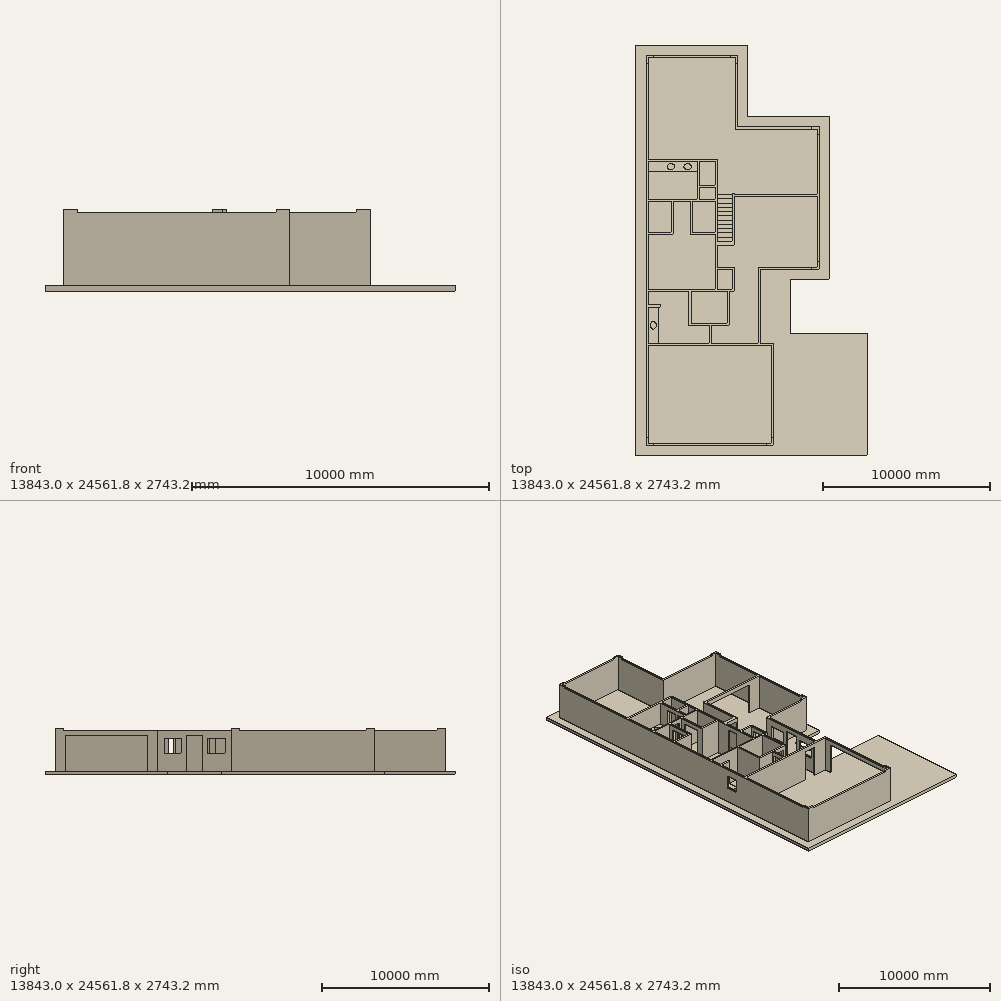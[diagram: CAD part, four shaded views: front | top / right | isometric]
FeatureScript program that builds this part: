
annotation { "Feature Type Name" : "Feature", "Feature Type Description" : "" }
export const myFeature = defineFeature(function(context is Context, id is Id, definition is map)
    precondition{}
    {
        {
            var Q0;
            Q0=qCreatedBy(makeId("Top.planeOp"),FACE);
            var sketch = newSketch(context, id + "F0", { "sketchPlane" : qUnion([Q0])});
            skLineSegment(sketch, "E0", {"start": v(0, 0) * mm, "end": v(7645.4, 0) * mm});
            skLineSegment(sketch, "E1", {"start": v(7645.4, 0) * mm, "end": v(7645.4, 6096) * mm});
            skLineSegment(sketch, "E2", {"start": v(7645.4, 6096) * mm, "end": v(6832.6, 6096) * mm});
            skLineSegment(sketch, "E3", {"start": v(6832.6, 6096) * mm, "end": v(6832.6, 10541) * mm});
            skLineSegment(sketch, "E4", {"start": v(6832.6, 10541) * mm, "end": v(10363.2, 10541) * mm});
            skLineSegment(sketch, "E5", {"start": v(10363.2, 10541) * mm, "end": v(10363.2, 19075.4) * mm});
            skLineSegment(sketch, "E6", {"start": v(10363.2, 19075.4) * mm, "end": v(5486.4, 19075.4) * mm});
            skLineSegment(sketch, "E7", {"start": v(5486.4, 19075.4) * mm, "end": v(5486.4, 23342.6) * mm});
            skLineSegment(sketch, "E8", {"start": v(5486.4, 23342.6) * mm, "end": v(0, 23342.6) * mm});
            skLineSegment(sketch, "E9", {"start": v(0, 23342.6) * mm, "end": v(0, 0) * mm});
            skSolve(sketch);
        }
        {
            var Q0;
            Q0 = qSketchRegion(id + "F0", true);
            extrude(context, id + "F1", {"entities" : qUnion([Q0]), "depth" : 2641.6 * mm});
        }
        {
            var Q0;
            Q0=qCreatedBy(makeId("Top.planeOp"),FACE);
            var sketch = newSketch(context, id + "F2", { "sketchPlane" : qUnion([Q0])});
            skLineSegment(sketch, "E10", {"start": v(-609.6, 23952.2) * mm, "end": v(-609.6, -609.6) * mm});
            skLineSegment(sketch, "E11", {"start": v(-609.6, -609.6) * mm, "end": v(13233.4, -609.6) * mm});
            skLineSegment(sketch, "E12", {"start": v(13233.4, -609.6) * mm, "end": v(13233.4, 6705.6) * mm});
            skLineSegment(sketch, "E13", {"start": v(13233.4, 6705.6) * mm, "end": v(8661.4, 6705.6) * mm});
            skLineSegment(sketch, "E14", {"start": v(8661.4, 6705.6) * mm, "end": v(8661.4, 9931.4) * mm});
            skLineSegment(sketch, "E15", {"start": v(8661.4, 9931.4) * mm, "end": v(10972.8, 9931.4) * mm});
            skLineSegment(sketch, "E16", {"start": v(10972.8, 9931.4) * mm, "end": v(10972.8, 19685) * mm});
            skLineSegment(sketch, "E17", {"start": v(10972.8, 19685) * mm, "end": v(6096, 19685) * mm});
            skLineSegment(sketch, "E18", {"start": v(6096, 19685) * mm, "end": v(6096, 23952.2) * mm});
            skLineSegment(sketch, "E19", {"start": v(6096, 23952.2) * mm, "end": v(-609.6, 23952.2) * mm});
            skSolve(sketch);
        }
        {
            var Q0;
            Q0 = qSketchRegion(id + "F2", true);
            extrude(context, id + "F3", {"entities" : qUnion([Q0]), "operationType" : NewBodyOperationType.ADD, "depth" : 203.2 * mm});
        }
        {
            var Q0;
            Q0=makeQuery(id+"F1.opExtrude","CAP_FACE",FACE,{"disambiguationData":[OSD([sQuery(id+"F0.wireOp",EDGE,"E0"),sQuery(id+"F0.wireOp",EDGE,"E1"),sQuery(id+"F0.wireOp",EDGE,"E2"),sQuery(id+"F0.wireOp",EDGE,"E3"),sQuery(id+"F0.wireOp",EDGE,"E4"),sQuery(id+"F0.wireOp",EDGE,"E5"),sQuery(id+"F0.wireOp",EDGE,"E6"),sQuery(id+"F0.wireOp",EDGE,"E7"),sQuery(id+"F0.wireOp",EDGE,"E8"),sQuery(id+"F0.wireOp",EDGE,"E9")])],"isStart":false});
            var sketch = newSketch(context, id + "F4", { "sketchPlane" : qUnion([Q0])});
            skLineSegment(sketch, "E20.bottom", {"start": v(127, 23215.6) * mm, "end": v(5359.4, 23215.6) * mm});
            skLineSegment(sketch, "E20.left", {"start": v(127, 23215.6) * mm, "end": v(127, 17119.6) * mm});
            skLineSegment(sketch, "E20.right", {"start": v(5359.4, 23215.6) * mm, "end": v(5359.4, 18948.4) * mm});
            skLineSegment(sketch, "E21.bottom", {"start": v(127, 5969) * mm, "end": v(7518.4, 5969) * mm});
            skLineSegment(sketch, "E21.top", {"start": v(127, 127) * mm, "end": v(7518.4, 127) * mm});
            skLineSegment(sketch, "E21.left", {"start": v(127, 5969) * mm, "end": v(127, 127) * mm});
            skLineSegment(sketch, "E21.right", {"start": v(7518.4, 5969) * mm, "end": v(7518.4, 127) * mm});
            skLineSegment(sketch, "E22", {"start": v(5359.4, 18948.4) * mm, "end": v(10236.2, 18948.4) * mm});
            skLineSegment(sketch, "E23", {"start": v(127, 17119.6) * mm, "end": v(4267.2, 17119.6) * mm});
            skLineSegment(sketch, "E24", {"start": v(4267.2, 17119.6) * mm, "end": v(4267.2, 10668) * mm});
            skLineSegment(sketch, "E25", {"start": v(4267.2, 10668) * mm, "end": v(5308.6, 10668) * mm});
            skLineSegment(sketch, "E26", {"start": v(10236.2, 10668) * mm, "end": v(10236.2, 14884.4) * mm});
            skLineSegment(sketch, "E27", {"start": v(5181.6, 15062.2) * mm, "end": v(5181.6, 11963.4) * mm});
            skLineSegment(sketch, "E28", {"start": v(5181.6, 11963.4) * mm, "end": v(5308.6, 11963.4) * mm});
            skLineSegment(sketch, "E29", {"start": v(5308.6, 11963.4) * mm, "end": v(5308.6, 14884.4) * mm});
            skLineSegment(sketch, "E30", {"start": v(5308.6, 14884.4) * mm, "end": v(10236.2, 14884.4) * mm});
            skLineSegment(sketch, "E31", {"start": v(5181.6, 15062.2) * mm, "end": v(5308.6, 15062.2) * mm});
            skLineSegment(sketch, "E32", {"start": v(5308.6, 15062.2) * mm, "end": v(5308.6, 15011.4) * mm});
            skLineSegment(sketch, "E33", {"start": v(5308.6, 15011.4) * mm, "end": v(10236.2, 15011.4) * mm});
            skLineSegment(sketch, "E34.trimOffspring", {"start": v(10236.2, 15011.4) * mm, "end": v(10236.2, 18948.4) * mm});
            skLineSegment(sketch, "E35.bottom", {"start": v(4140.2, 16992.6) * mm, "end": v(3225.8, 16992.6) * mm});
            skLineSegment(sketch, "E35.top", {"start": v(4140.2, 15570.2) * mm, "end": v(3225.8, 15570.2) * mm});
            skLineSegment(sketch, "E35.left", {"start": v(4140.2, 16992.6) * mm, "end": v(4140.2, 15570.2) * mm});
            skLineSegment(sketch, "E35.right", {"start": v(3225.8, 16992.6) * mm, "end": v(3225.8, 15570.2) * mm});
            skLineSegment(sketch, "E36.bottom", {"start": v(127, 16992.6) * mm, "end": v(3098.8, 16992.6) * mm});
            skLineSegment(sketch, "E36.top", {"start": v(127, 14706.6) * mm, "end": v(3098.8, 14706.6) * mm});
            skLineSegment(sketch, "E36.left", {"start": v(127, 16992.6) * mm, "end": v(127, 14706.6) * mm});
            skLineSegment(sketch, "E36.right", {"start": v(3098.8, 16992.6) * mm, "end": v(3098.8, 14706.6) * mm});
            skLineSegment(sketch, "E37.bottom", {"start": v(127, 14579.6) * mm, "end": v(1498.6, 14579.6) * mm});
            skLineSegment(sketch, "E37.top", {"start": v(127, 12750.8) * mm, "end": v(1498.6, 12750.8) * mm});
            skLineSegment(sketch, "E37.left", {"start": v(127, 14579.6) * mm, "end": v(127, 12750.8) * mm});
            skLineSegment(sketch, "E37.right", {"start": v(1498.6, 14579.6) * mm, "end": v(1498.6, 12750.8) * mm});
            skLineSegment(sketch, "E38.bottom", {"start": v(2768.6, 14579.6) * mm, "end": v(4140.2, 14579.6) * mm});
            skLineSegment(sketch, "E38.top", {"start": v(2768.6, 12750.8) * mm, "end": v(4140.2, 12750.8) * mm});
            skLineSegment(sketch, "E38.left", {"start": v(2768.6, 14579.6) * mm, "end": v(2768.6, 12750.8) * mm});
            skLineSegment(sketch, "E38.right", {"start": v(4140.2, 14579.6) * mm, "end": v(4140.2, 12750.8) * mm});
            skLineSegment(sketch, "E39", {"start": v(2641.6, 12623.8) * mm, "end": v(2641.6, 14579.6) * mm});
            skLineSegment(sketch, "E40", {"start": v(2641.6, 14579.6) * mm, "end": v(1625.6, 14579.6) * mm});
            skLineSegment(sketch, "E41", {"start": v(1625.6, 14579.6) * mm, "end": v(1625.6, 12623.8) * mm});
            skLineSegment(sketch, "E42", {"start": v(1625.6, 12623.8) * mm, "end": v(127, 12623.8) * mm});
            skLineSegment(sketch, "E43", {"start": v(2641.6, 12623.8) * mm, "end": v(4140.2, 12623.8) * mm});
            skLineSegment(sketch, "E44.bottom", {"start": v(4267.2, 10541) * mm, "end": v(5181.6, 10541) * mm});
            skLineSegment(sketch, "E44.top", {"start": v(4267.2, 9321.8) * mm, "end": v(5181.6, 9321.8) * mm});
            skLineSegment(sketch, "E44.left", {"start": v(4267.2, 10541) * mm, "end": v(4267.2, 9321.8) * mm});
            skLineSegment(sketch, "E44.right", {"start": v(5181.6, 10541) * mm, "end": v(5181.6, 9321.8) * mm});
            skLineSegment(sketch, "E45.right", {"start": v(2692.4, 9194.8) * mm, "end": v(2692.4, 7289.8) * mm});
            skLineSegment(sketch, "E46", {"start": v(4140.2, 12623.8) * mm, "end": v(4140.2, 9321.8) * mm});
            skLineSegment(sketch, "E47", {"start": v(4140.2, 9321.8) * mm, "end": v(127, 9321.8) * mm});
            skLineSegment(sketch, "E48", {"start": v(127, 9321.8) * mm, "end": v(127, 12623.8) * mm});
            skLineSegment(sketch, "E49", {"start": v(3784.6, 6096) * mm, "end": v(127, 6096) * mm});
            skLineSegment(sketch, "E50", {"start": v(127, 6096) * mm, "end": v(127, 8280.4) * mm});
            skLineSegment(sketch, "E51", {"start": v(127, 9194.8) * mm, "end": v(2565.4, 9194.8) * mm});
            skLineSegment(sketch, "E52", {"start": v(2565.4, 9194.8) * mm, "end": v(2565.4, 7162.8) * mm});
            skLineSegment(sketch, "E53", {"start": v(2565.4, 7162.8) * mm, "end": v(3784.6, 7162.8) * mm});
            skLineSegment(sketch, "E54", {"start": v(3784.6, 7162.8) * mm, "end": v(3784.6, 6096) * mm});
            skLineSegment(sketch, "E55", {"start": v(3911.6, 7162.8) * mm, "end": v(3911.6, 6096) * mm});
            skLineSegment(sketch, "E56", {"start": v(3911.6, 6096) * mm, "end": v(6705.6, 6096) * mm});
            skLineSegment(sketch, "E57", {"start": v(6705.6, 6096) * mm, "end": v(6705.6, 10668) * mm});
            skLineSegment(sketch, "E58", {"start": v(3911.6, 7162.8) * mm, "end": v(5003.8, 7162.8) * mm});
            skLineSegment(sketch, "E59", {"start": v(5308.6, 9194.8) * mm, "end": v(5308.6, 10668) * mm});
            skLineSegment(sketch, "E60.trimOffspring", {"start": v(6705.6, 10668) * mm, "end": v(10236.2, 10668) * mm});
            skLineSegment(sketch, "E61.bottom", {"start": v(3225.8, 15443.2) * mm, "end": v(4140.2, 15443.2) * mm});
            skLineSegment(sketch, "E61.top", {"start": v(3225.8, 14706.6) * mm, "end": v(4140.2, 14706.6) * mm});
            skLineSegment(sketch, "E61.left", {"start": v(3225.8, 15443.2) * mm, "end": v(3225.8, 14706.6) * mm});
            skLineSegment(sketch, "E61.right", {"start": v(4140.2, 15443.2) * mm, "end": v(4140.2, 14706.6) * mm});
            skLineSegment(sketch, "E62", {"start": v(127, 8407.4) * mm, "end": v(889, 8407.4) * mm});
            skLineSegment(sketch, "E63", {"start": v(889, 8407.4) * mm, "end": v(889, 8280.4) * mm});
            skLineSegment(sketch, "E64", {"start": v(889, 8280.4) * mm, "end": v(127, 8280.4) * mm});
            skLineSegment(sketch, "E65.trimOffspring", {"start": v(127, 8407.4) * mm, "end": v(127, 9194.8) * mm});
            skLineSegment(sketch, "E66", {"start": v(2692.4, 9194.8) * mm, "end": v(4876.8, 9194.8) * mm});
            skLineSegment(sketch, "E67", {"start": v(4876.8, 9194.8) * mm, "end": v(4876.8, 7289.8) * mm});
            skLineSegment(sketch, "E68", {"start": v(4876.8, 7289.8) * mm, "end": v(2692.4, 7289.8) * mm});
            skLineSegment(sketch, "E69", {"start": v(5003.8, 7162.8) * mm, "end": v(5003.8, 9194.8) * mm});
            skLineSegment(sketch, "E70", {"start": v(5003.8, 9194.8) * mm, "end": v(5308.6, 9194.8) * mm});
            skSolve(sketch);
        }
        {
            var Q0;
            Q0 = qSketchRegion(id + "F4", true);
            extrude(context, id + "F5", {"entities" : qUnion([Q0]), "operationType" : NewBodyOperationType.REMOVE, "oppositeDirection" : true, "depth" : 2438.4 * mm});
        }
        {
            var Q0;
            Q0=makeQuery(id+"F5.boolean.opBoolean","COPY",FACE,{"derivedFrom":makeQuery(id+"F5.opExtrude","SWEPT_FACE",FACE,{"disambiguationData":[OSD([sQuery(id+"F4.wireOp",EDGE,"E24")])]})});
            var sketch = newSketch(context, id + "F6", { "sketchPlane" : qUnion([Q0])});
            skLineSegment(sketch, "E71", {"start": v(14757.4, 203.2) * mm, "end": v(15011.4, 203.2) * mm});
            skLineSegment(sketch, "E72", {"start": v(15011.4, 203.2) * mm, "end": v(15011.4, 406.4) * mm});
            skLineSegment(sketch, "E73", {"start": v(15011.4, 406.4) * mm, "end": v(14757.4, 406.4) * mm});
            skLineSegment(sketch, "E74", {"start": v(14757.4, 406.4) * mm, "end": v(14757.4, 609.6) * mm});
            skLineSegment(sketch, "E75", {"start": v(14757.4, 609.6) * mm, "end": v(14503.4, 609.6) * mm});
            skLineSegment(sketch, "E76", {"start": v(14503.4, 609.6) * mm, "end": v(14503.4, 812.8) * mm});
            skLineSegment(sketch, "E77", {"start": v(14503.4, 812.8) * mm, "end": v(14249.4, 812.8) * mm});
            skLineSegment(sketch, "E78", {"start": v(14249.4, 812.8) * mm, "end": v(14249.4, 1016) * mm});
            skLineSegment(sketch, "E79", {"start": v(14249.4, 1016) * mm, "end": v(13995.4, 1016) * mm});
            skLineSegment(sketch, "E80", {"start": v(13995.4, 1016) * mm, "end": v(13995.4, 1219.2) * mm});
            skLineSegment(sketch, "E81", {"start": v(13995.4, 1219.2) * mm, "end": v(13741.4, 1219.2) * mm});
            skLineSegment(sketch, "E82", {"start": v(13741.4, 1219.2) * mm, "end": v(13741.4, 1422.4) * mm});
            skLineSegment(sketch, "E83", {"start": v(13741.4, 1422.4) * mm, "end": v(13487.4, 1422.4) * mm});
            skLineSegment(sketch, "E84", {"start": v(13487.4, 1422.4) * mm, "end": v(13487.4, 1625.6) * mm});
            skLineSegment(sketch, "E85", {"start": v(13487.4, 1625.6) * mm, "end": v(13233.4, 1625.6) * mm});
            skLineSegment(sketch, "E86", {"start": v(13233.4, 1625.6) * mm, "end": v(13233.4, 1828.8) * mm});
            skLineSegment(sketch, "E87", {"start": v(13233.4, 1828.8) * mm, "end": v(12979.4, 1828.8) * mm});
            skLineSegment(sketch, "E88", {"start": v(12979.4, 1828.8) * mm, "end": v(12979.4, 2032) * mm});
            skLineSegment(sketch, "E89", {"start": v(12979.4, 2032) * mm, "end": v(12725.4, 2032) * mm});
            skLineSegment(sketch, "E90", {"start": v(12725.4, 2032) * mm, "end": v(12725.4, 2235.2) * mm});
            skLineSegment(sketch, "E91", {"start": v(12725.4, 2235.2) * mm, "end": v(12471.4, 2235.2) * mm});
            skLineSegment(sketch, "E92", {"start": v(12471.4, 2235.2) * mm, "end": v(12471.4, 2438.4) * mm});
            skLineSegment(sketch, "E93", {"start": v(12471.4, 2438.4) * mm, "end": v(12217.4, 2438.4) * mm});
            skLineSegment(sketch, "E94", {"start": v(12217.4, 2438.4) * mm, "end": v(12217.4, 2641.6) * mm});
            skLineSegment(sketch, "E95", {"start": v(12217.4, 2641.6) * mm, "end": v(11963.4, 2641.6) * mm});
            skLineSegment(sketch, "E96", {"start": v(11963.4, 2641.6) * mm, "end": v(11963.4, 2387.6) * mm});
            skLineSegment(sketch, "E97", {"start": v(11963.4, 2387.6) * mm, "end": v(14757.4, 203.2) * mm});
            skSolve(sketch);
        }
        {
            var Q0;
            Q0 = qSketchRegion(id + "F6", true);
            extrude(context, id + "F7", {"entities" : qUnion([Q0]), "operationType" : NewBodyOperationType.ADD, "endBound" : BoundingType.UP_TO_NEXT, "depth" : 25.4 * mm});
        }
        {
            var Q0;
            Q0=makeQuery(id+"F5.boolean.opBoolean","COPY",FACE,{"derivedFrom":makeQuery(id+"F5.opExtrude","SWEPT_FACE",FACE,{"disambiguationData":[OSD([sQuery(id+"F4.wireOp",EDGE,"E21.right")])]})});
            var sketch = newSketch(context, id + "F8", { "sketchPlane" : qUnion([Q0])});
            skLineSegment(sketch, "E98.bottom", {"start": v(-5486.4, 203.2) * mm, "end": v(-609.6, 203.2) * mm});
            skLineSegment(sketch, "E98.top", {"start": v(-5486.4, 2336.8) * mm, "end": v(-609.6, 2336.8) * mm});
            skLineSegment(sketch, "E98.left", {"start": v(-5486.4, 203.2) * mm, "end": v(-5486.4, 2336.8) * mm});
            skLineSegment(sketch, "E98.right", {"start": v(-609.6, 203.2) * mm, "end": v(-609.6, 2336.8) * mm});
            skLineSegment(sketch, "E99", {"start": v(-3048, 2641.6) * mm, "end": v(-3048, 203.2) * mm, "construction": true});
            skSolve(sketch);
        }
        {
            var Q0;
            Q0 = qSketchRegion(id + "F8", true);
            extrude(context, id + "F9", {"entities" : qUnion([Q0]), "operationType" : NewBodyOperationType.REMOVE, "endBound" : BoundingType.UP_TO_NEXT, "oppositeDirection" : true, "depth" : 25.4 * mm});
        }
        {
            var Q0;
            Q0=makeQuery(id+"F5.boolean.opBoolean","COPY",FACE,{"derivedFrom":makeQuery(id+"F5.opExtrude","SWEPT_FACE",FACE,{"disambiguationData":[OSD([sQuery(id+"F4.wireOp",EDGE,"E30")])]})});
            var sketch = newSketch(context, id + "F10", { "sketchPlane" : qUnion([Q0])});
            skLineSegment(sketch, "E100.bottom", {"start": v(5461, 203.2) * mm, "end": v(9372.6, 203.2) * mm});
            skLineSegment(sketch, "E100.top", {"start": v(5461, 2336.8) * mm, "end": v(9372.6, 2336.8) * mm});
            skLineSegment(sketch, "E100.left", {"start": v(5461, 203.2) * mm, "end": v(5461, 2336.8) * mm});
            skLineSegment(sketch, "E100.right", {"start": v(9372.6, 203.2) * mm, "end": v(9372.6, 2336.8) * mm});
            skSolve(sketch);
        }
        {
            var Q0;
            Q0 = qSketchRegion(id + "F10", true);
            extrude(context, id + "F11", {"entities" : qUnion([Q0]), "operationType" : NewBodyOperationType.REMOVE, "endBound" : BoundingType.UP_TO_NEXT, "oppositeDirection" : true, "depth" : 25.4 * mm});
        }
        {
            var Q0;
            Q0=makeQuery(id+"F5.boolean.opBoolean","COPY",FACE,{"derivedFrom":makeQuery(id+"F5.opExtrude","CAP_FACE",FACE,{"disambiguationData":[OSD([sQuery(id+"F4.wireOp",EDGE,"E36.bottom"),sQuery(id+"F4.wireOp",EDGE,"E36.top"),sQuery(id+"F4.wireOp",EDGE,"E36.left"),sQuery(id+"F4.wireOp",EDGE,"E36.right")])],"isStart":false})});
            var sketch = newSketch(context, id + "F12", { "sketchPlane" : qUnion([Q0])});
            skLineSegment(sketch, "E101.bottom", {"start": v(127, 16992.6) * mm, "end": v(3098.8, 16992.6) * mm});
            skLineSegment(sketch, "E101.top", {"start": v(127, 16383) * mm, "end": v(3098.8, 16383) * mm});
            skLineSegment(sketch, "E101.left", {"start": v(127, 16992.6) * mm, "end": v(127, 16383) * mm});
            skLineSegment(sketch, "E101.right", {"start": v(3098.8, 16992.6) * mm, "end": v(3098.8, 16383) * mm});
            skSolve(sketch);
        }
        {
            var Q0;
            Q0 = qSketchRegion(id + "F12", true);
            extrude(context, id + "F13", {"entities" : qUnion([Q0]), "operationType" : NewBodyOperationType.ADD, "depth" : 838.2 * mm});
        }
        {
            var Q0;
            Q0=makeQuery(id+"F13.opExtrude","CAP_FACE",FACE,{"disambiguationData":[OSD([sQuery(id+"F12.wireOp",EDGE,"E101.bottom"),sQuery(id+"F12.wireOp",EDGE,"E101.top"),sQuery(id+"F12.wireOp",EDGE,"E101.left"),sQuery(id+"F12.wireOp",EDGE,"E101.right")])],"isStart":false});
            var sketch = newSketch(context, id + "F14", { "sketchPlane" : qUnion([Q0])});
            skLineSegment(sketch, "E102", {"start": v(2489.2, 16992.6) * mm, "end": v(2489.2, 16383) * mm, "construction": true});
            skLineSegment(sketch, "E103", {"start": v(1498.6, 16992.6) * mm, "end": v(1498.6, 16383) * mm, "construction": true});
            skEllipse(sketch, "E104", {"center": v(2489.2, 16687.8) * mm, "majorRadius": 228.6 * mm, "minorRadius": 177.8 * mm, "majorAxis": v(-1, 0)});
            skEllipse(sketch, "E105", {"center": v(1498.6, 16687.8) * mm, "majorRadius": 228.6 * mm, "minorRadius": 177.8 * mm, "majorAxis": v(-1, 0)});
            skSolve(sketch);
        }
        {
            var Q0;
            Q0 = qSketchRegion(id + "F14", true);
            extrude(context, id + "F15", {"entities" : qUnion([Q0]), "operationType" : NewBodyOperationType.REMOVE, "oppositeDirection" : true, "depth" : 304.8 * mm});
        }
        {
            var Q0;
            Q0=makeQuery(id+"F5.boolean.opBoolean","COPY",FACE,{"derivedFrom":makeQuery(id+"F5.opExtrude","CAP_FACE",FACE,{"disambiguationData":[OSD([sQuery(id+"F4.wireOp",EDGE,"E49"),sQuery(id+"F4.wireOp",EDGE,"E50"),sQuery(id+"F4.wireOp",EDGE,"E51"),sQuery(id+"F4.wireOp",EDGE,"E52"),sQuery(id+"F4.wireOp",EDGE,"E53"),sQuery(id+"F4.wireOp",EDGE,"E54")])],"isStart":false})});
            var sketch = newSketch(context, id + "F16", { "sketchPlane" : qUnion([Q0])});
            skLineSegment(sketch, "E106.bottom", {"start": v(127, 6096) * mm, "end": v(736.6, 6096) * mm});
            skLineSegment(sketch, "E106.top", {"start": v(127, 8280.4) * mm, "end": v(736.6, 8280.4) * mm});
            skLineSegment(sketch, "E106.left", {"start": v(127, 6096) * mm, "end": v(127, 8280.4) * mm});
            skLineSegment(sketch, "E106.right", {"start": v(736.6, 6096) * mm, "end": v(736.6, 8280.4) * mm});
            skSolve(sketch);
        }
        {
            var Q0;
            Q0 = qSketchRegion(id + "F16", true);
            extrude(context, id + "F17", {"entities" : qUnion([Q0]), "operationType" : NewBodyOperationType.ADD, "depth" : 838.2 * mm});
        }
        {
            var Q0;
            Q0=makeQuery(id+"F17.opExtrude","CAP_FACE",FACE,{"disambiguationData":[OSD([sQuery(id+"F16.wireOp",EDGE,"E106.bottom"),sQuery(id+"F16.wireOp",EDGE,"E106.top"),sQuery(id+"F16.wireOp",EDGE,"E106.left"),sQuery(id+"F16.wireOp",EDGE,"E106.right")])],"isStart":false});
            var sketch = newSketch(context, id + "F18", { "sketchPlane" : qUnion([Q0])});
            skLineSegment(sketch, "E107", {"start": v(127, 7188.2) * mm, "end": v(736.6, 7188.2) * mm, "construction": true});
            skEllipse(sketch, "E108", {"center": v(431.8, 7188.2) * mm, "majorRadius": 228.6 * mm, "minorRadius": 177.8 * mm, "majorAxis": v(0, 1)});
            skSolve(sketch);
        }
        {
            var Q0;
            Q0 = qSketchRegion(id + "F18", true);
            extrude(context, id + "F19", {"entities" : qUnion([Q0]), "operationType" : NewBodyOperationType.REMOVE, "oppositeDirection" : true, "depth" : 304.8 * mm});
        }
        {
            var Q0;
            Q0=makeQuery(id+"F1.opExtrude","SWEPT_FACE",FACE,{"disambiguationData":[OSD([sQuery(id+"F0.wireOp",EDGE,"E3")])]});
            var sketch = newSketch(context, id + "F20", { "sketchPlane" : qUnion([Q0])});
            skLineSegment(sketch, "E109.bottom", {"start": v(7861.3, 203.2) * mm, "end": v(8775.7, 203.2) * mm});
            skLineSegment(sketch, "E109.top", {"start": v(7861.3, 2336.8) * mm, "end": v(8775.7, 2336.8) * mm});
            skLineSegment(sketch, "E109.left", {"start": v(7861.3, 203.2) * mm, "end": v(7861.3, 2336.8) * mm});
            skLineSegment(sketch, "E109.right", {"start": v(8775.7, 203.2) * mm, "end": v(8775.7, 2336.8) * mm});
            skLineSegment(sketch, "E110", {"start": v(8318.5, 2641.6) * mm, "end": v(8318.5, 203.2) * mm, "construction": true});
            skLineSegment(sketch, "E111.bottom", {"start": v(6489.7, 2159) * mm, "end": v(7556.5, 2159) * mm});
            skLineSegment(sketch, "E111.top", {"start": v(6489.7, 1244.6) * mm, "end": v(7556.5, 1244.6) * mm});
            skLineSegment(sketch, "E111.left", {"start": v(6489.7, 2159) * mm, "end": v(6489.7, 1244.6) * mm});
            skLineSegment(sketch, "E111.right", {"start": v(7556.5, 2159) * mm, "end": v(7556.5, 1244.6) * mm});
            skLineSegment(sketch, "E112.MirrorCS", {"start": v(10147.3, 2159) * mm, "end": v(9080.5, 2159) * mm});
            skLineSegment(sketch, "E113.MirrorCS", {"start": v(10147.3, 1244.6) * mm, "end": v(9080.5, 1244.6) * mm});
            skLineSegment(sketch, "E114.MirrorCS", {"start": v(10147.3, 2159) * mm, "end": v(10147.3, 1244.6) * mm});
            skLineSegment(sketch, "E115.MirrorCS", {"start": v(9080.5, 2159) * mm, "end": v(9080.5, 1244.6) * mm});
            skSolve(sketch);
        }
        {
            var Q0;
            Q0 = qSketchRegion(id + "F20", true);
            extrude(context, id + "F21", {"entities" : qUnion([Q0]), "operationType" : NewBodyOperationType.REMOVE, "endBound" : BoundingType.UP_TO_NEXT, "oppositeDirection" : true, "depth" : 25.4 * mm});
        }
        {
            var Q0;
            Q0=makeQuery(id+"F5.boolean.opBoolean","COPY",FACE,{"derivedFrom":makeQuery(id+"F5.opExtrude","SWEPT_FACE",FACE,{"disambiguationData":[OSD([sQuery(id+"F4.wireOp",EDGE,"E56")])]})});
            var sketch = newSketch(context, id + "F22", { "sketchPlane" : qUnion([Q0])});
            skLineSegment(sketch, "E116.bottom", {"start": v(-6553.2, 203.2) * mm, "end": v(-5638.8, 203.2) * mm});
            skLineSegment(sketch, "E116.top", {"start": v(-6553.2, 2336.8) * mm, "end": v(-5638.8, 2336.8) * mm});
            skLineSegment(sketch, "E116.left", {"start": v(-6553.2, 203.2) * mm, "end": v(-6553.2, 2336.8) * mm});
            skLineSegment(sketch, "E116.right", {"start": v(-5638.8, 203.2) * mm, "end": v(-5638.8, 2336.8) * mm});
            skSolve(sketch);
        }
        {
            var Q0;
            Q0 = qSketchRegion(id + "F22", true);
            extrude(context, id + "F23", {"entities" : qUnion([Q0]), "operationType" : NewBodyOperationType.REMOVE, "endBound" : BoundingType.UP_TO_NEXT, "oppositeDirection" : true, "depth" : 25.4 * mm});
        }
        {
            var Q0;
            Q0=makeQuery(id+"F5.boolean.opBoolean","COPY",FACE,{"derivedFrom":makeQuery(id+"F5.opExtrude","SWEPT_FACE",FACE,{"disambiguationData":[OSD([sQuery(id+"F4.wireOp",EDGE,"E58")])]})});
            var sketch = newSketch(context, id + "F24", { "sketchPlane" : qUnion([Q0])});
            skLineSegment(sketch, "E117.bottom", {"start": v(4013.2, 203.2) * mm, "end": v(4775.2, 203.2) * mm});
            skLineSegment(sketch, "E117.top", {"start": v(4013.2, 2336.8) * mm, "end": v(4775.2, 2336.8) * mm});
            skLineSegment(sketch, "E117.left", {"start": v(4013.2, 203.2) * mm, "end": v(4013.2, 2336.8) * mm});
            skLineSegment(sketch, "E117.right", {"start": v(4775.2, 203.2) * mm, "end": v(4775.2, 2336.8) * mm});
            skSolve(sketch);
        }
        {
            var Q0;
            Q0 = qSketchRegion(id + "F24", true);
            extrude(context, id + "F25", {"entities" : qUnion([Q0]), "operationType" : NewBodyOperationType.REMOVE, "endBound" : BoundingType.UP_TO_NEXT, "oppositeDirection" : true, "depth" : 25.4 * mm});
        }
        {
            var Q0;
            Q0=makeQuery(id+"F5.boolean.opBoolean","COPY",FACE,{"derivedFrom":makeQuery(id+"F5.opExtrude","SWEPT_FACE",FACE,{"disambiguationData":[OSD([sQuery(id+"F4.wireOp",EDGE,"E55")])]})});
            var sketch = newSketch(context, id + "F26", { "sketchPlane" : qUnion([Q0])});
            skLineSegment(sketch, "E118.bottom", {"start": v(7048.5, 203.2) * mm, "end": v(6286.5, 203.2) * mm});
            skLineSegment(sketch, "E118.top", {"start": v(7048.5, 2336.8) * mm, "end": v(6286.5, 2336.8) * mm});
            skLineSegment(sketch, "E118.left", {"start": v(7048.5, 203.2) * mm, "end": v(7048.5, 2336.8) * mm});
            skLineSegment(sketch, "E118.right", {"start": v(6286.5, 203.2) * mm, "end": v(6286.5, 2336.8) * mm});
            skSolve(sketch);
        }
        {
            var Q0;
            Q0 = qSketchRegion(id + "F26", true);
            extrude(context, id + "F27", {"entities" : qUnion([Q0]), "operationType" : NewBodyOperationType.REMOVE, "endBound" : BoundingType.UP_TO_NEXT, "oppositeDirection" : true, "depth" : 25.4 * mm});
        }
        {
            var Q0;
            Q0=makeQuery(id+"F5.boolean.opBoolean","COPY",FACE,{"derivedFrom":makeQuery(id+"F5.opExtrude","SWEPT_FACE",FACE,{"disambiguationData":[OSD([sQuery(id+"F4.wireOp",EDGE,"E50")])]})});
            var sketch = newSketch(context, id + "F28", { "sketchPlane" : qUnion([Q0])});
            skLineSegment(sketch, "E119.bottom", {"start": v(6731, 2159) * mm, "end": v(7645.4, 2159) * mm});
            skLineSegment(sketch, "E119.top", {"start": v(6731, 1244.6) * mm, "end": v(7645.4, 1244.6) * mm});
            skLineSegment(sketch, "E119.left", {"start": v(6731, 2159) * mm, "end": v(6731, 1244.6) * mm});
            skLineSegment(sketch, "E119.right", {"start": v(7645.4, 2159) * mm, "end": v(7645.4, 1244.6) * mm});
            skLineSegment(sketch, "E120", {"start": v(7188.2, 2641.6) * mm, "end": v(7188.2, 1041.4) * mm, "construction": true});
            skSolve(sketch);
        }
        {
            var Q0;
            Q0 = qSketchRegion(id + "F28", true);
            extrude(context, id + "F29", {"entities" : qUnion([Q0]), "operationType" : NewBodyOperationType.REMOVE, "endBound" : BoundingType.UP_TO_NEXT, "oppositeDirection" : true, "depth" : 25.4 * mm});
        }
        {
            var Q0;
            Q0=makeQuery(id+"F5.boolean.opBoolean","COPY",FACE,{"derivedFrom":makeQuery(id+"F5.opExtrude","SWEPT_FACE",FACE,{"disambiguationData":[OSD([sQuery(id+"F4.wireOp",EDGE,"E59")])]})});
            var sketch = newSketch(context, id + "F30", { "sketchPlane" : qUnion([Q0])});
            skLineSegment(sketch, "E121.bottom", {"start": v(9550.4, 203.2) * mm, "end": v(10312.4, 203.2) * mm});
            skLineSegment(sketch, "E121.top", {"start": v(9550.4, 2336.8) * mm, "end": v(10312.4, 2336.8) * mm});
            skLineSegment(sketch, "E121.left", {"start": v(9550.4, 203.2) * mm, "end": v(9550.4, 2336.8) * mm});
            skLineSegment(sketch, "E121.right", {"start": v(10312.4, 203.2) * mm, "end": v(10312.4, 2336.8) * mm});
            skSolve(sketch);
        }
        {
            var Q0;
            Q0 = qSketchRegion(id + "F30", true);
            extrude(context, id + "F31", {"entities" : qUnion([Q0]), "operationType" : NewBodyOperationType.REMOVE, "endBound" : BoundingType.UP_TO_NEXT, "oppositeDirection" : true, "depth" : 25.4 * mm});
        }
        {
            var Q0;
            {var subQ0=sQuery(id+"F4.wireOp",EDGE,"E25");var subQ2=sQuery(id+"F4.wireOp",EDGE,"E24");Q0=makeQuery(id+"F7.boolean.opBoolean","SPLIT",FACE,{"disambiguationData":[TD([makeQuery(id+"F5.boolean.opBoolean","COPY",FACE,{"derivedFrom":makeQuery(id+"F5.opExtrude","SWEPT_FACE",FACE,{"disambiguationData":[OSD([subQ0])]})})])],"derivedFrom":makeQuery(id+"F5.boolean.opBoolean","COPY",FACE,{"derivedFrom":makeQuery(id+"F5.opExtrude","SWEPT_FACE",FACE,{"disambiguationData":[OSD([subQ2])]})})});}
            var sketch = newSketch(context, id + "F32", { "sketchPlane" : qUnion([Q0])});
            skLineSegment(sketch, "E122.bottom", {"start": v(10922, 203.2) * mm, "end": v(11684, 203.2) * mm});
            skLineSegment(sketch, "E122.top", {"start": v(10922, 2336.8) * mm, "end": v(11684, 2336.8) * mm});
            skLineSegment(sketch, "E122.left", {"start": v(10922, 203.2) * mm, "end": v(10922, 2336.8) * mm});
            skLineSegment(sketch, "E122.right", {"start": v(11684, 203.2) * mm, "end": v(11684, 2336.8) * mm});
            skSolve(sketch);
        }
        {
            var Q0;
            Q0 = qSketchRegion(id + "F32", true);
            extrude(context, id + "F33", {"entities" : qUnion([Q0]), "operationType" : NewBodyOperationType.REMOVE, "endBound" : BoundingType.UP_TO_NEXT, "oppositeDirection" : true, "depth" : 25.4 * mm});
        }
        {
            var Q0;
            Q0=makeQuery(id+"F5.boolean.opBoolean","COPY",FACE,{"derivedFrom":makeQuery(id+"F5.opExtrude","SWEPT_FACE",FACE,{"disambiguationData":[OSD([sQuery(id+"F4.wireOp",EDGE,"E38.left")])]})});
            var sketch = newSketch(context, id + "F34", { "sketchPlane" : qUnion([Q0])});
            skLineSegment(sketch, "E123", {"start": v(13665.2, 2641.6) * mm, "end": v(13665.2, 203.2) * mm, "construction": true});
            skLineSegment(sketch, "E124.bottom", {"start": v(14274.8, 203.2) * mm, "end": v(13055.6, 203.2) * mm});
            skLineSegment(sketch, "E124.top", {"start": v(14274.8, 2336.8) * mm, "end": v(13055.6, 2336.8) * mm});
            skLineSegment(sketch, "E124.left", {"start": v(14274.8, 203.2) * mm, "end": v(14274.8, 2336.8) * mm});
            skLineSegment(sketch, "E124.right", {"start": v(13055.6, 203.2) * mm, "end": v(13055.6, 2336.8) * mm});
            skSolve(sketch);
        }
        {
            var Q0;
            Q0 = qSketchRegion(id + "F34", true);
            var Q1;
            Q1=makeQuery(id+"F5.boolean.opBoolean","COPY",FACE,{"derivedFrom":makeQuery(id+"F5.opExtrude","SWEPT_FACE",FACE,{"disambiguationData":[OSD([sQuery(id+"F4.wireOp",EDGE,"E37.right")])]})});
            extrude(context, id + "F35", {"entities" : qUnion([Q0]), "operationType" : NewBodyOperationType.REMOVE, "endBound" : BoundingType.UP_TO_SURFACE, "oppositeDirection" : true, "endBoundEntityFace" : qUnion([Q1]), "depth" : 25.4 * mm});
        }
        {
            var Q0;
            Q0=makeQuery(id+"F5.boolean.opBoolean","COPY",FACE,{"derivedFrom":makeQuery(id+"F5.opExtrude","SWEPT_FACE",FACE,{"disambiguationData":[OSD([sQuery(id+"F4.wireOp",EDGE,"E40")])]})});
            var sketch = newSketch(context, id + "F36", { "sketchPlane" : qUnion([Q0])});
            skLineSegment(sketch, "E125", {"start": v(2133.6, 203.2) * mm, "end": v(2133.6, 2641.6) * mm, "construction": true});
            skLineSegment(sketch, "E126.bottom", {"start": v(1752.6, 203.2) * mm, "end": v(2514.6, 203.2) * mm});
            skLineSegment(sketch, "E126.top", {"start": v(1752.6, 2336.8) * mm, "end": v(2514.6, 2336.8) * mm});
            skLineSegment(sketch, "E126.left", {"start": v(1752.6, 203.2) * mm, "end": v(1752.6, 2336.8) * mm});
            skLineSegment(sketch, "E126.right", {"start": v(2514.6, 203.2) * mm, "end": v(2514.6, 2336.8) * mm});
            skSolve(sketch);
        }
        {
            var Q0;
            Q0 = qSketchRegion(id + "F36", true);
            extrude(context, id + "F37", {"entities" : qUnion([Q0]), "operationType" : NewBodyOperationType.REMOVE, "endBound" : BoundingType.UP_TO_NEXT, "oppositeDirection" : true, "depth" : 25.4 * mm});
        }
        {
            var Q0;
            Q0=makeQuery(id+"F5.boolean.opBoolean","COPY",FACE,{"derivedFrom":makeQuery(id+"F5.opExtrude","SWEPT_FACE",FACE,{"disambiguationData":[OSD([sQuery(id+"F4.wireOp",EDGE,"E36.right")])]})});
            var sketch = newSketch(context, id + "F38", { "sketchPlane" : qUnion([Q0])});
            skLineSegment(sketch, "E127.bottom", {"start": v(-15621, 203.2) * mm, "end": v(-16281.4, 203.2) * mm});
            skLineSegment(sketch, "E127.top", {"start": v(-15621, 2336.8) * mm, "end": v(-16281.4, 2336.8) * mm});
            skLineSegment(sketch, "E127.left", {"start": v(-15621, 203.2) * mm, "end": v(-15621, 2336.8) * mm});
            skLineSegment(sketch, "E127.right", {"start": v(-16281.4, 203.2) * mm, "end": v(-16281.4, 2336.8) * mm});
            skLineSegment(sketch, "E128.bottom", {"start": v(-15379.7, 203.2) * mm, "end": v(-14770.1, 203.2) * mm});
            skLineSegment(sketch, "E128.top", {"start": v(-15379.7, 2336.8) * mm, "end": v(-14770.1, 2336.8) * mm});
            skLineSegment(sketch, "E128.left", {"start": v(-15379.7, 203.2) * mm, "end": v(-15379.7, 2336.8) * mm});
            skLineSegment(sketch, "E128.right", {"start": v(-14770.1, 203.2) * mm, "end": v(-14770.1, 2336.8) * mm});
            skSolve(sketch);
        }
        {
            var Q0;
            Q0 = qSketchRegion(id + "F38", true);
            extrude(context, id + "F39", {"entities" : qUnion([Q0]), "operationType" : NewBodyOperationType.REMOVE, "endBound" : BoundingType.UP_TO_NEXT, "oppositeDirection" : true, "depth" : 25.4 * mm});
        }
        {
            var Q0;
            Q0=makeQuery(id+"F7.boolean.opBoolean","MERGE",FACE,{"derivedFrom":[makeQuery(id+"F1.opExtrude","CAP_FACE",FACE,{"disambiguationData":[OSD([sQuery(id+"F0.wireOp",EDGE,"E0"),sQuery(id+"F0.wireOp",EDGE,"E1"),sQuery(id+"F0.wireOp",EDGE,"E2"),sQuery(id+"F0.wireOp",EDGE,"E3"),sQuery(id+"F0.wireOp",EDGE,"E4"),sQuery(id+"F0.wireOp",EDGE,"E5"),sQuery(id+"F0.wireOp",EDGE,"E6"),sQuery(id+"F0.wireOp",EDGE,"E7"),sQuery(id+"F0.wireOp",EDGE,"E8"),sQuery(id+"F0.wireOp",EDGE,"E9")])],"isStart":false}),makeQuery(id+"F7.opExtrude","SWEPT_FACE",FACE,{"disambiguationData":[OSD([sQuery(id+"F6.wireOp",EDGE,"E95")])]})]});
            var sketch = newSketch(context, id + "F40", { "sketchPlane" : qUnion([Q0])});
            skLineSegment(sketch, "E129", {"start": v(0, 0) * mm, "end": v(0, 457.2) * mm});
            skLineSegment(sketch, "E130", {"start": v(0, 457.2) * mm, "end": v(127, 457.2) * mm});
            skLineSegment(sketch, "E131", {"start": v(127, 457.2) * mm, "end": v(127, 127) * mm});
            skLineSegment(sketch, "E132", {"start": v(127, 127) * mm, "end": v(457.2, 127) * mm});
            skLineSegment(sketch, "E133", {"start": v(457.2, 127) * mm, "end": v(457.2, 0) * mm});
            skLineSegment(sketch, "E134", {"start": v(457.2, 0) * mm, "end": v(0, 0) * mm});
            skLineSegment(sketch, "E135", {"start": v(7645.4, 0) * mm, "end": v(7188.2, 0) * mm});
            skLineSegment(sketch, "E136", {"start": v(7188.2, 0) * mm, "end": v(7188.2, 127) * mm});
            skLineSegment(sketch, "E137", {"start": v(7188.2, 127) * mm, "end": v(7518.4, 127) * mm});
            skLineSegment(sketch, "E138", {"start": v(7518.4, 127) * mm, "end": v(7518.4, 457.2) * mm});
            skLineSegment(sketch, "E139", {"start": v(7518.4, 457.2) * mm, "end": v(7645.4, 457.2) * mm});
            skLineSegment(sketch, "E140", {"start": v(7645.4, 457.2) * mm, "end": v(7645.4, 0) * mm});
            skLineSegment(sketch, "E141", {"start": v(10363.2, 10541) * mm, "end": v(9906, 10541) * mm});
            skLineSegment(sketch, "E142", {"start": v(9906, 10541) * mm, "end": v(9906, 10668) * mm});
            skLineSegment(sketch, "E143", {"start": v(9906, 10668) * mm, "end": v(10236.2, 10668) * mm});
            skLineSegment(sketch, "E144", {"start": v(10236.2, 10668) * mm, "end": v(10236.2, 10998.2) * mm});
            skLineSegment(sketch, "E145", {"start": v(10236.2, 10998.2) * mm, "end": v(10363.2, 10998.2) * mm});
            skLineSegment(sketch, "E146", {"start": v(10363.2, 10998.2) * mm, "end": v(10363.2, 10541) * mm});
            skLineSegment(sketch, "E147", {"start": v(10363.2, 19075.4) * mm, "end": v(10363.2, 18618.2) * mm});
            skLineSegment(sketch, "E148", {"start": v(10363.2, 18618.2) * mm, "end": v(10236.2, 18618.2) * mm});
            skLineSegment(sketch, "E149", {"start": v(10236.2, 18618.2) * mm, "end": v(10236.2, 18948.4) * mm});
            skLineSegment(sketch, "E150", {"start": v(10236.2, 18948.4) * mm, "end": v(9906, 18948.4) * mm});
            skLineSegment(sketch, "E151", {"start": v(9906, 18948.4) * mm, "end": v(9906, 19075.4) * mm});
            skLineSegment(sketch, "E152", {"start": v(9906, 19075.4) * mm, "end": v(10363.2, 19075.4) * mm});
            skLineSegment(sketch, "E153", {"start": v(0, 22885.4) * mm, "end": v(0, 23342.6) * mm});
            skLineSegment(sketch, "E154", {"start": v(0, 23342.6) * mm, "end": v(457.2, 23342.6) * mm});
            skLineSegment(sketch, "E155", {"start": v(457.2, 23342.6) * mm, "end": v(457.2, 23215.6) * mm});
            skLineSegment(sketch, "E156", {"start": v(457.2, 23215.6) * mm, "end": v(127, 23215.6) * mm});
            skLineSegment(sketch, "E157", {"start": v(127, 23215.6) * mm, "end": v(127, 22885.4) * mm});
            skLineSegment(sketch, "E158", {"start": v(127, 22885.4) * mm, "end": v(0, 22885.4) * mm});
            skLineSegment(sketch, "E159", {"start": v(5486.4, 23342.6) * mm, "end": v(5029.2, 23342.6) * mm});
            skLineSegment(sketch, "E160", {"start": v(5029.2, 23342.6) * mm, "end": v(5029.2, 23215.6) * mm});
            skLineSegment(sketch, "E161", {"start": v(5029.2, 23215.6) * mm, "end": v(5359.4, 23215.6) * mm});
            skLineSegment(sketch, "E162", {"start": v(5359.4, 23215.6) * mm, "end": v(5359.4, 22885.4) * mm});
            skLineSegment(sketch, "E163", {"start": v(5359.4, 22885.4) * mm, "end": v(5486.4, 22885.4) * mm});
            skLineSegment(sketch, "E164", {"start": v(5486.4, 22885.4) * mm, "end": v(5486.4, 23342.6) * mm});
            skSolve(sketch);
        }
        {
            var Q0;
            Q0 = qSketchRegion(id + "F40", true);
            extrude(context, id + "F41", {"entities" : qUnion([Q0]), "operationType" : NewBodyOperationType.ADD, "depth" : 101.6 * mm});
        }
    });
